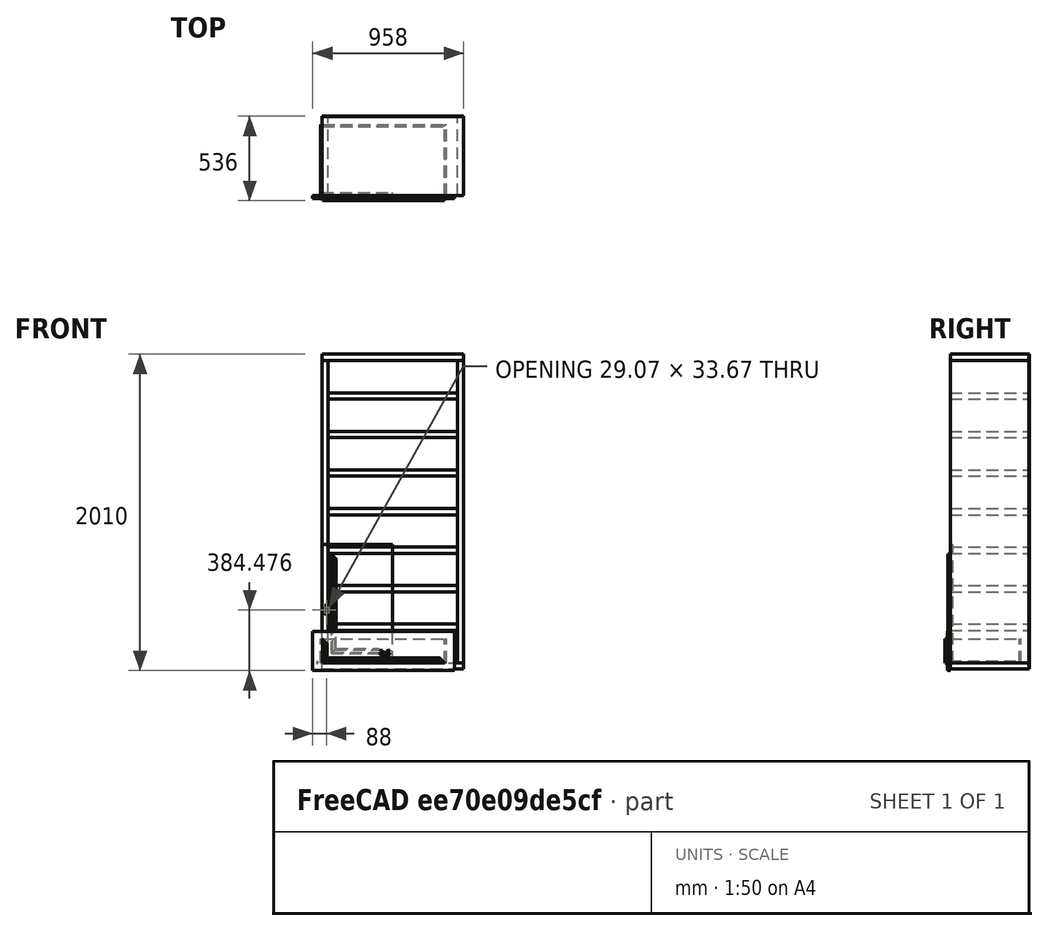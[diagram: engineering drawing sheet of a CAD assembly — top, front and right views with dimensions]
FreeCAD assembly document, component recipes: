
FREECAD ASSEMBLY — COMPONENT RECIPES ("Merged_002")

This assembly document has 18 components, labeled P0..P17 below (a component is one placed body or linked part). 9 of them carry a construction recipe — the FreeCAD feature program that regenerates the part from scratch, quoted from this document or its linked companion documents; the rest are supplied as boundary geometry only. No exploded tour is included for this assembly.
COMPONENT P0 — geometry summary ("Handle, Pin, Right"; no construction recipe available for this part):
  bounding box: 17.0 x 10.0 x 10.0 mm
  tessellated surface: 1,802 triangles
  volume: 817 mm^3 (48% of its bounding box)
  symmetry: revolution-symmetric about the y axis through its bounding-box center; mirror-symmetric across its x mid-plane, z mid-plane
COMPONENT P1 — geometry summary ("Link, Decoration, Top"; no construction recipe available for this part):
  bounding box: 776.0 x 30.0 x 15.0 mm
  tessellated surface: 126 triangles
  volume: 161274 mm^3 (46% of its bounding box)
  symmetry: mirror-symmetric across its x mid-plane
COMPONENT P2 — geometry summary ("Link, Decoration, Right"; no construction recipe available for this part):
  bounding box: 150.0 x 30.0 x 15.0 mm
  tessellated surface: 124 triangles
  volume: 27059 mm^3 (40% of its bounding box)
  symmetry: mirror-symmetric across its z mid-plane
COMPONENT P3 — geometry summary ("Link, Drawer"; no construction recipe available for this part):
  bounding box: 900.0 x 485.0 x 250.0 mm
  tessellated surface: 4,788 triangles
  volume: 8497740 mm^3 (8% of its bounding box)
  symmetry: mirror-symmetric across its x mid-plane
COMPONENT P4 — geometry summary ("Link, Segment 2"; no construction recipe available for this part):
  bounding box: 2000.0 x 901.0 x 538.0 mm
  tessellated surface: 15,092 triangles
  volume: 262938344 mm^3 (27% of its bounding box)
  symmetry: mirror-symmetric across its x mid-plane
COMPONENT P5 — geometry summary ("Link, Decoration, Top001"; no construction recipe available for this part):
  bounding box: 330.0 x 30.0 x 15.0 mm
  tessellated surface: 126 triangles
  volume: 65652 mm^3 (44% of its bounding box)
  symmetry: mirror-symmetric across its x mid-plane
COMPONENT P6 — geometry summary ("Link, Decoration, Right001"; no construction recipe available for this part):
  bounding box: 630.0 x 30.0 x 15.0 mm
  tessellated surface: 124 triangles
  volume: 129972 mm^3 (46% of its bounding box)
  symmetry: mirror-symmetric across its z mid-plane
COMPONENT P7 — geometry summary ("Link, Decoration, Top002"; no construction recipe available for this part):
  bounding box: 330.0 x 30.0 x 15.0 mm
  tessellated surface: 126 triangles
  volume: 65652 mm^3 (44% of its bounding box)
  symmetry: mirror-symmetric across its x mid-plane
COMPONENT P8 — geometry summary ("Link, Decoration, Right002"; no construction recipe available for this part):
  bounding box: 630.0 x 30.0 x 15.0 mm
  tessellated surface: 124 triangles
  volume: 129972 mm^3 (46% of its bounding box)
  symmetry: mirror-symmetric across its z mid-plane
COMPONENT P9 — recipe-attached ("Part, Handle", modeled in this document).
Construction recipe (the document's own serialized feature program — sketch geometry with constraints, then the solid features built on it; lengths are millimeters unless a unit is written):

FEATURE [Sketcher::SketchObject] Sketch006  label="Pattern, Handle"
  ArcFitTolerance = 0
  AttachmentOffset = pos=(400,75,28) rot=(0,0,1;0rad)
  AttachmentSupport = -> [XZ_Plane006]
  ExternalTypes = [0]
  FullyConstrained = true
  MakeInternals = false
  MapMode = 5
  Placement = pos=(400,-28,75) rot=(1,0,0;1.5708rad)
  _ExternalGeoVersion = 0
  expr: .AttachmentOffset.Base.x = <<settings>>.dwidth / 2
  expr: .AttachmentOffset.Base.y = <<settings>>.dheight / 2
  expr: .AttachmentOffset.Base.z = <<settings>>.fthick + 10 mm
  sketch-geometry (20):
    g0: LineSegment StartX=-31.5 StartY=2.62 StartZ=0 EndX=-17.57 EndY=2.62 EndZ=0
    g1: LineSegment StartX=-31.5 StartY=0 StartZ=0 EndX=-17.3512 EndY=0 EndZ=0
    g2: LineSegment StartX=-16.85 StartY=-2.15 StartZ=0 EndX=-28.7075 EndY=-12.82 EndZ=0
    g3: LineSegment StartX=-15.2654 StartY=-4.11 StartZ=0 EndX=-25.6265 EndY=-16.59 EndZ=0
    g4: LineSegment StartX=15.2654 StartY=-4.11 StartZ=0 EndX=25.6265 EndY=-16.59 EndZ=0
    g5: LineSegment StartX=16.85 StartY=-2.15 StartZ=0 EndX=28.7075 EndY=-12.82 EndZ=0
    g6: LineSegment StartX=17.57 StartY=2.62 StartZ=0 EndX=31.5 EndY=2.62 EndZ=0
    g7: LineSegment StartX=17.3512 StartY=0 StartZ=0 EndX=31.5 EndY=0 EndZ=0
    g8: LineSegment StartX=-10.78 StartY=-22.72 StartZ=0 EndX=10.78 EndY=-22.72 EndZ=0
    g9: LineSegment StartX=-31.5 StartY=2.62 StartZ=0 EndX=-31.5 EndY=0 EndZ=0
    g10: LineSegment StartX=31.5 StartY=2.62 StartZ=0 EndX=31.5 EndY=0 EndZ=0
    g11: ArcOfCircle CenterX=-17.98 CenterY=-1.28 CenterZ=0 NormalX=0 NormalY=0 NormalZ=1 AngleXU=0 Radius=3.92149 StartAngle=5.47698 EndAngle=7.74924
    g12: ArcOfCircle CenterX=-17.98 CenterY=-1.28 CenterZ=0 NormalX=0 NormalY=0 NormalZ=1 AngleXU=0 Radius=1.42611 StartAngle=5.62706 EndAngle=7.39735
    g13: ArcOfCircle CenterX=-19.81 CenterY=-17.89 CenterZ=0 NormalX=0 NormalY=0 NormalZ=1 AngleXU=0 Radius=10.2406 StartAngle=2.62366 EndAngle=5.79202
    g14: ArcOfCircle CenterX=19.81 CenterY=-17.89 CenterZ=0 NormalX=0 NormalY=0 NormalZ=1 AngleXU=0 Radius=10.2406 StartAngle=3.63276 EndAngle=6.80112
    g15: ArcOfCircle CenterX=17.98 CenterY=-1.28 CenterZ=0 NormalX=0 NormalY=0 NormalZ=1 AngleXU=0 Radius=3.92149 StartAngle=1.67554 EndAngle=3.9478
    g16: ArcOfCircle CenterX=17.98 CenterY=-1.28 CenterZ=0 NormalX=0 NormalY=0 NormalZ=1 AngleXU=0 Radius=1.42611 StartAngle=2.02742 EndAngle=3.79772
    g17: ArcOfCircle CenterX=0 CenterY=-24.02 CenterZ=0 NormalX=0 NormalY=0 NormalZ=1 AngleXU=0 Radius=14.7824 StartAngle=0.285269 EndAngle=2.85632
    g18: ArcOfCircle CenterX=-19.81 CenterY=-17.89 CenterZ=0 NormalX=0 NormalY=0 NormalZ=1 AngleXU=0 Radius=5.95999 StartAngle=2.9217 EndAngle=5.94631
    g19: ArcOfCircle CenterX=19.81 CenterY=-17.89 CenterZ=0 NormalX=0 NormalY=0 NormalZ=1 AngleXU=0 Radius=5.95999 StartAngle=3.47847 EndAngle=6.50307
  constraints (66):
    c: Horizontal(g0)
    c: Horizontal(g1)
    c: Horizontal(g6)
    c: Horizontal(g7)
    c: Horizontal(g8)
    c: Coincident(g9,g0)
    c: Coincident(g9,g1)
    c: Vertical(g9)
    c: Coincident(g10,g6)
    c: Vertical(g10)
    c: Coincident(g10,g7)
    c: Coincident(g11,g0)
    c: Coincident(g11,g3)
    c: Coincident(g12,g1)
    c: Coincident(g12,g2)
    c: Coincident(g13,g2)
    c: Coincident(g13,g8)
    c: Coincident(g14,g5)
    c: Coincident(g14,g8)
    c: Coincident(g15,g4)
    c: Coincident(g15,g6)
    c: Coincident(g16,g7)
    c: Coincident(g16,g5)
    c: Coincident(g18,g3)
    c: Coincident(g18,g17)
    c: Coincident(g19,g17)
    c: Coincident(g19,g4)
    c: Coincident(g15,g16)
    c: Coincident(g11,g12)
    c: Horizontal(g2,g5)
    c: Horizontal(g3,g4)
    c: Horizontal(g0,g6)
    c: Horizontal(g1,g7)
    c: Horizontal(g5,g2)
    c: Horizontal(g13,g14)
    c: Horizontal(g18,g19)
    c: Horizontal(g17,g17)
    c: Horizontal(g3,g4)
    c: PointOnObject(g17,g-2)
    c: Equal(g11,g15)
    c: Equal(g0,g6)
    c: Equal(g1,g7)
    c: Equal(g3,g4)
    c: Equal(g18,g19)
    c: Equal(g2,g5)
    c: Equal(g13,g14)
    c: Horizontal(g11,g15)
    c: Coincident(g13,g18)
    c: PointOnObject(g7,g-1)
    c: DistanceY(g17,g-1) = 24.02
    c: DistanceY(g14,g-1) = 17.89
    c: DistanceY(g2,g-1) = 12.82
    c: DistanceY(g3,g-1) = 16.59
    c: DistanceY(g8,g-1) = 22.72
    c: DistanceX(g8,g-1) = 10.78
    c: DistanceY(g3,g-1) = 4.11
    c: DistanceY(g2,g-1) = 2.15
    c: DistanceY(g-1,g0) = 2.62
    c: DistanceX(g0,g6) = 63
    c: DistanceX(g13,g14) = 39.62
    c: DistanceX(g17,g17) = 28.37
    c: DistanceY(g17,g-1) = 19.86
    c: DistanceX(g11,g-1) = 17.98
    c: DistanceX(g0,g-1) = 17.57
    c: DistanceX(g2,g-1) = 16.85
    c: DistanceY(g11,g-1) = 1.28
FEATURE [PartDesign::Pad] Pad006  label="Handle"
  Direction = (0,-1,2e-16)
  Length = 5
  Length2 = 10
  Placement = pos=(0,0,0) rot=(1,0,0;1.5708rad)
  Profile = -> Sketch006
  ReferenceAxis = -> Sketch006 [N_Axis]
  SideType = 0
  Suppressed = false
  Type = 0
  Type2 = 0
FEATURE [PartDesign::Body] Body006  label="Body, Handle"
  AllowCompound = true
  Group = -> [Sketch006,Pad006]
  Origin = -> Origin007
  Tip = -> Pad006
COMPONENT P10 — recipe-attached ("Part, Decoration, Bottom", modeled in this document).
Construction recipe (the document's own serialized feature program — sketch geometry with constraints, then the solid features built on it; lengths are millimeters unless a unit is written):

FEATURE [Sketcher::SketchObject] Sketch  label="Pattern, Decoration, Bottom"
  ArcFitTolerance = 0
  AttachmentOffset = pos=(-18,0,4) rot=(0,0,1;0rad)
  AttachmentSupport = -> [YZ_Plane008]
  ExternalTypes = [0]
  FullyConstrained = true
  MakeInternals = false
  MapMode = 5
  Placement = pos=(4,-18,0) rot=(0.57735,0.57735,0.57735;2.0944rad)
  _ExternalGeoVersion = 0
  expr: .AttachmentOffset.Base.x = -<<settings>>.fthick
  expr: .AttachmentOffset.Base.z = <<settings>>.bsink
  sketch-geometry (5):
    g0: LineSegment StartX=4e-16 StartY=30 StartZ=0 EndX=4e-16 EndY=0 EndZ=0
    g1: LineSegment StartX=4e-16 StartY=0 StartZ=0 EndX=-15 EndY=0 EndZ=0
    g2: ArcOfCircle CenterX=0 CenterY=23 CenterZ=0 NormalX=0 NormalY=0 NormalZ=1 AngleXU=0 Radius=7 StartAngle=1.5708 EndAngle=3.14159
    g3: ArcOfCircle CenterX=-16.3537 CenterY=15.4828 CenterZ=0 NormalX=0 NormalY=0 NormalZ=1 AngleXU=0 Radius=12 StartAngle=5.372 EndAngle=6.96016
    g4: ArcOfCircle CenterX=-9 CenterY=0 CenterZ=0 NormalX=0 NormalY=0 NormalZ=1 AngleXU=0 Radius=6 StartAngle=1.5708 EndAngle=3.14159
  constraints (17):
    c: Vertical(g0)
    c: Coincident(g1,g0)
    c: Horizontal(g1)
    c: Coincident(g2,g0)
    c: Coincident(g3,g2)
    c: Coincident(g4,g3)
    c: Coincident(g4,g1)
    c: DistanceY(g0,g0) = 30
    c: DistanceX(g1,g1) = 15
    c: Coincident(g0,g-1)
    c: PointOnObject(g2,g0)
    c: PointOnObject(g4,g1)
    c: Radius(g2) = 7
    c: Radius(g3) = 12
    c: Radius(g4) = 6
    c: Vertical(g3,g4)
    c: Horizontal(g2,g2)
FEATURE [PartDesign::Pad] Pad  label="Decoration, Bottom"
  Direction = (1,0,0)
  Length = 776
  Length2 = 10
  Placement = pos=(0,0,0) rot=(0.57735,0.57735,0.57735;2.0944rad)
  Profile = -> Sketch
  ReferenceAxis = -> Sketch [N_Axis]
  SideType = 0
  Suppressed = false
  Type = 0
  Type2 = 0
  expr: Length = <<settings>>.dwidth - 2 * <<settings>>.dthick
FEATURE [PartDesign::Body] Body  label="Body, Decoration, Bottom"
  AllowCompound = true
  Group = -> [Sketch,Pad]
  Origin = -> Origin009
  Tip = -> Pad
FEATURE [Sketcher::SketchObject] Sketch007  label="Pattern, Decoration, Bottom, Cut, Left"
  ArcFitTolerance = 0
  AttachmentOffset = pos=(4,0,18) rot=(0,0,1;0rad)
  AttachmentSupport = -> [XZ_Plane009]
  ExternalTypes = [0]
  FullyConstrained = true
  MakeInternals = false
  MapMode = 5
  Placement = pos=(4,-18,4e-15) rot=(1,0,0;1.5708rad)
  _ExternalGeoVersion = 0
  expr: .AttachmentOffset.Base.x = <<settings>>.bsink
  expr: .AttachmentOffset.Base.z = <<settings>>.fthick
  sketch-geometry (3):
    g0: LineSegment StartX=0 StartY=0 StartZ=0 EndX=40 EndY=40 EndZ=0
    g1: LineSegment StartX=40 StartY=40 StartZ=0 EndX=0 EndY=40 EndZ=0
    g2: LineSegment StartX=0 StartY=40 StartZ=0 EndX=0 EndY=0 EndZ=0
  constraints (8):
    c: Coincident(g0,g1)
    c: Horizontal(g1)
    c: Coincident(g1,g2)
    c: Coincident(g2,g0)
    c: Coincident(g0,g-1)
    c: Vertical(g2)
    c: Equal(g2,g1)
    c: DistanceY(g2,g2) = 40
FEATURE [PartDesign::Pad] Pad007  label="Decoration, Bottom, Cut, Left"
  Direction = (0,-1,2e-16)
  Length = 40
  Length2 = 10
  Placement = pos=(0,0,0) rot=(1,0,0;1.5708rad)
  Profile = -> Sketch007
  ReferenceAxis = -> Sketch007 [N_Axis]
  SideType = 0
  Suppressed = false
  Type = 0
  Type2 = 0
FEATURE [PartDesign::Body] Body007  label="Body, Decoration, Bottom, Cut, Left"
  AllowCompound = true
  Group = -> [Sketch007,Pad007]
  Origin = -> Origin010
  Tip = -> Pad007
FEATURE [Sketcher::SketchObject] Sketch008  label="Pattern, Decoration, Bottom, Cut, Right"
  ArcFitTolerance = 0
  AttachmentOffset = pos=(780,0,18) rot=(0,0,1;0rad)
  AttachmentSupport = -> [XZ_Plane010]
  ExternalTypes = [0]
  FullyConstrained = true
  MakeInternals = false
  MapMode = 5
  Placement = pos=(780,-18,4e-15) rot=(1,0,0;1.5708rad)
  _ExternalGeoVersion = 0
  expr: .AttachmentOffset.Base.x = <<settings>>.bsink + <<settings>>.dwidth - 2 * <<settings>>.dthick
  expr: .AttachmentOffset.Base.z = <<settings>>.fthick
  sketch-geometry (3):
    g0: LineSegment StartX=-40 StartY=40 StartZ=0 EndX=0 EndY=0 EndZ=0
    g1: LineSegment StartX=0 StartY=0 StartZ=0 EndX=0 EndY=40 EndZ=0
    g2: LineSegment StartX=0 StartY=40 StartZ=0 EndX=-40 EndY=40 EndZ=0
  constraints (8):
    c: Coincident(g0,g-1)
    c: Coincident(g0,g1)
    c: PointOnObject(g1,g-2)
    c: Coincident(g1,g2)
    c: Coincident(g2,g0)
    c: Horizontal(g2)
    c: Equal(g2,g1)
    c: DistanceY(g1,g1) = 40
FEATURE [PartDesign::Pad] Pad008  label="Decoration, Bottom, Cut, Right"
  Direction = (0,-1,2e-16)
  Length = 40
  Length2 = 10
  Placement = pos=(0,0,0) rot=(1,0,0;1.5708rad)
  Profile = -> Sketch008
  ReferenceAxis = -> Sketch008 [N_Axis]
  SideType = 0
  Suppressed = false
  Type = 0
  Type2 = 0
FEATURE [PartDesign::Body] Body008  label="Body, Decoration, Bottom, Cut, Right"
  AllowCompound = true
  Group = -> [Sketch008,Pad008]
  Origin = -> Origin011
  Tip = -> Pad008
COMPONENT P11 — recipe-attached ("Part, Decoration, Left", modeled in this document).
Construction recipe (the document's own serialized feature program — sketch geometry with constraints, then the solid features built on it; lengths are millimeters unless a unit is written):

FEATURE [Sketcher::SketchObject] Sketch009  label="Pattern, Decoration, Left"
  ArcFitTolerance = 0
  AttachmentOffset = pos=(4,-18,0) rot=(0,0,1;0rad)
  AttachmentSupport = -> [XY_Plane012]
  ExternalTypes = [0]
  FullyConstrained = true
  MakeInternals = false
  MapMode = 5
  Placement = pos=(4,-18,0) rot=(0,0,1;0rad)
  _ExternalGeoVersion = 0
  expr: .AttachmentOffset.Base.x = <<settings>>.bsink
  expr: .AttachmentOffset.Base.y = -<<settings>>.fthick
  sketch-geometry (5):
    g0: LineSegment StartX=30 StartY=-1.7e-15 StartZ=0 EndX=0 EndY=-1.7e-15 EndZ=0
    g1: LineSegment StartX=-1.1e-15 StartY=-15 StartZ=0 EndX=-1.1e-15 EndY=-1.8e-15 EndZ=0
    g2: ArcOfCircle CenterX=0 CenterY=-9 CenterZ=0 NormalX=0 NormalY=0 NormalZ=1 AngleXU=0 Radius=6 StartAngle=4.71239 EndAngle=6.28319
    g3: ArcOfCircle CenterX=15.4828 CenterY=-16.3537 CenterZ=0 NormalX=0 NormalY=0 NormalZ=1 AngleXU=0 Radius=12 StartAngle=0.893826 EndAngle=2.48198
    g4: ArcOfCircle CenterX=23 CenterY=0 CenterZ=0 NormalX=0 NormalY=0 NormalZ=1 AngleXU=0 Radius=7 StartAngle=4.71239 EndAngle=6.28319
  constraints (17):
    c: Vertical(g1)
    c: Coincident(g0,g1)
    c: Horizontal(g0)
    c: Coincident(g0,g-1)
    c: DistanceY(g1,g1) = 15
    c: DistanceX(g0,g0) = 30
    c: Coincident(g2,g1)
    c: Coincident(g3,g2)
    c: Coincident(g4,g3)
    c: Coincident(g4,g0)
    c: PointOnObject(g4,g0)
    c: PointOnObject(g2,g1)
    c: Radius(g2) = 6
    c: Radius(g3) = 12
    c: Radius(g4) = 7
    c: Horizontal(g2,g2)
    c: Vertical(g3,g4)
FEATURE [PartDesign::Pad] Pad009  label="Decoration, Left"
  Direction = (0,0,1)
  Length = 150
  Length2 = 10
  Profile = -> Sketch009
  ReferenceAxis = -> Sketch009 [N_Axis]
  SideType = 0
  Suppressed = false
  Type = 0
  Type2 = 0
  expr: Length = <<settings>>.dheight
FEATURE [PartDesign::Body] Body009  label="Body, Decoration, Left"
  AllowCompound = true
  Group = -> [Sketch009,Pad009]
  Origin = -> Origin013
  Tip = -> Pad009
FEATURE [Sketcher::SketchObject] Sketch010  label="Pattern, Decoration, Left, Cut, Bottom"
  ArcFitTolerance = 0
  AttachmentOffset = pos=(4,0,18) rot=(0,0,1;0rad)
  AttachmentSupport = -> [XZ_Plane013]
  ExternalTypes = [0]
  FullyConstrained = true
  MakeInternals = false
  MapMode = 5
  Placement = pos=(4,-18,4e-15) rot=(1,0,0;1.5708rad)
  _ExternalGeoVersion = 0
  expr: .AttachmentOffset.Base.x = <<settings>>.bsink
  expr: .AttachmentOffset.Base.z = <<settings>>.fthick
  sketch-geometry (3):
    g0: LineSegment StartX=0 StartY=0 StartZ=0 EndX=40 EndY=40 EndZ=0
    g1: LineSegment StartX=40 StartY=40 StartZ=0 EndX=40 EndY=0 EndZ=0
    g2: LineSegment StartX=40 StartY=0 StartZ=0 EndX=0 EndY=0 EndZ=0
  constraints (8):
    c: Coincident(g-1,g0)
    c: Coincident(g0,g1)
    c: PointOnObject(g1,g-1)
    c: Vertical(g1)
    c: Coincident(g1,g2)
    c: Coincident(g2,g0)
    c: Equal(g1,g2)
    c: DistanceY(g1,g1) = 40
FEATURE [PartDesign::Pad] Pad010  label="Decoration, Left, Cut, Bottom"
  Direction = (0,-1,2e-16)
  Length = 40
  Length2 = 10
  Placement = pos=(0,0,0) rot=(1,0,0;1.5708rad)
  Profile = -> Sketch010
  ReferenceAxis = -> Sketch010 [N_Axis]
  SideType = 0
  Suppressed = false
  Type = 0
  Type2 = 0
FEATURE [PartDesign::Body] Body010  label="Body, Decoration, Left, Cut, Bottom"
  AllowCompound = true
  Group = -> [Sketch010,Pad010]
  Origin = -> Origin014
  Tip = -> Pad010
FEATURE [Sketcher::SketchObject] Sketch011  label="Pattern, Decoration, Left, Cut, Top"
  ArcFitTolerance = 0
  AttachmentOffset = pos=(4,150,18) rot=(0,0,1;0rad)
  AttachmentSupport = -> [XZ_Plane014]
  ExternalTypes = [0]
  FullyConstrained = true
  MakeInternals = false
  MapMode = 5
  Placement = pos=(4,-18,150) rot=(1,0,0;1.5708rad)
  _ExternalGeoVersion = 0
  expr: .AttachmentOffset.Base.x = <<settings>>.bsink
  expr: .AttachmentOffset.Base.y = <<settings>>.dheight
  expr: .AttachmentOffset.Base.z = <<settings>>.fthick
  sketch-geometry (3):
    g0: LineSegment StartX=0 StartY=0 StartZ=0 EndX=40 EndY=-40 EndZ=0
    g1: LineSegment StartX=40 StartY=-40 StartZ=0 EndX=40 EndY=0 EndZ=0
    g2: LineSegment StartX=40 StartY=0 StartZ=0 EndX=0 EndY=0 EndZ=0
  constraints (8):
    c: Coincident(g-1,g0)
    c: Coincident(g0,g1)
    c: PointOnObject(g1,g-1)
    c: Vertical(g1)
    c: Coincident(g1,g2)
    c: Coincident(g2,g0)
    c: Equal(g1,g2)
    c: DistanceY(g1,g1) = 40
FEATURE [PartDesign::Pad] Pad011  label="Decoration, Left, Cut, Top"
  Direction = (0,-1,2e-16)
  Length = 40
  Length2 = 10
  Placement = pos=(0,0,0) rot=(1,0,0;1.5708rad)
  Profile = -> Sketch011
  ReferenceAxis = -> Sketch011 [N_Axis]
  SideType = 0
  Suppressed = false
  Type = 0
  Type2 = 0
FEATURE [PartDesign::Body] Body011  label="Body, Decoration, Left, Cut, Top"
  AllowCompound = true
  Group = -> [Sketch011,Pad011]
  Origin = -> Origin015
  Tip = -> Pad011
COMPONENT P12 — recipe-attached ("Part, Decoration, Bottom001", modeled in this document).
Construction recipe (the document's own serialized feature program — sketch geometry with constraints, then the solid features built on it; lengths are millimeters unless a unit is written):

FEATURE [Sketcher::SketchObject] Sketch012  label="Pattern, Decoration, Bottom001"
  ArcFitTolerance = 0
  AttachmentOffset = pos=(0,60,60) rot=(0,0,1;0rad)
  AttachmentSupport = -> [YZ_Plane016]
  ExternalTypes = [0]
  FullyConstrained = true
  MakeInternals = false
  MapMode = 5
  Placement = pos=(60,0,60) rot=(0.57735,0.57735,0.57735;2.0944rad)
  _ExternalGeoVersion = 0
  expr: .AttachmentOffset.Base.y = Spreadsheet001.frdoffset
  expr: .AttachmentOffset.Base.z = Spreadsheet001.frdoffset
  sketch-geometry (5):
    g0: LineSegment StartX=4e-16 StartY=30 StartZ=0 EndX=4e-16 EndY=0 EndZ=0
    g1: LineSegment StartX=4e-16 StartY=0 StartZ=0 EndX=-15 EndY=0 EndZ=0
    g2: ArcOfCircle CenterX=0 CenterY=23 CenterZ=0 NormalX=0 NormalY=0 NormalZ=1 AngleXU=0 Radius=7 StartAngle=1.5708 EndAngle=3.14159
    g3: ArcOfCircle CenterX=-16.3537 CenterY=15.4828 CenterZ=0 NormalX=0 NormalY=0 NormalZ=1 AngleXU=0 Radius=12 StartAngle=5.372 EndAngle=6.96016
    g4: ArcOfCircle CenterX=-9 CenterY=0 CenterZ=0 NormalX=0 NormalY=0 NormalZ=1 AngleXU=0 Radius=6 StartAngle=1.5708 EndAngle=3.14159
  constraints (17):
    c: Vertical(g0)
    c: Coincident(g1,g0)
    c: Horizontal(g1)
    c: Coincident(g2,g0)
    c: Coincident(g3,g2)
    c: Coincident(g4,g3)
    c: Coincident(g4,g1)
    c: DistanceY(g0,g0) = 30
    c: DistanceX(g1,g1) = 15
    c: Coincident(g0,g-1)
    c: PointOnObject(g2,g0)
    c: PointOnObject(g4,g1)
    c: Radius(g2) = 7
    c: Radius(g3) = 12
    c: Radius(g4) = 6
    c: Vertical(g3,g4)
    c: Horizontal(g2,g2)
FEATURE [PartDesign::Pad] Pad012  label="Decoration, Bottom001"
  Direction = (1,0,0)
  Length = 330
  Length2 = 10
  Placement = pos=(0,0,0) rot=(0.57735,0.57735,0.57735;2.0944rad)
  Profile = -> Sketch012
  ReferenceAxis = -> Sketch012 [N_Axis]
  SideType = 0
  Suppressed = false
  Type = 0
  Type2 = 0
  expr: Length = Spreadsheet001.frfwidth - 2 * Spreadsheet001.frdoffset
FEATURE [PartDesign::Body] Body012  label="Body, Decoration, Bottom001"
  AllowCompound = true
  Group = -> [Sketch012,Pad012]
  Origin = -> Origin017
  Tip = -> Pad012
FEATURE [Sketcher::SketchObject] Sketch013  label="Pattern, Decoration, Bottom, Cut, Left001"
  ArcFitTolerance = 0
  AttachmentOffset = pos=(60,60,0) rot=(0,0,1;0rad)
  AttachmentSupport = -> [XZ_Plane017]
  ExternalTypes = [0]
  FullyConstrained = true
  MakeInternals = false
  MapMode = 5
  Placement = pos=(60,1.33e-14,60) rot=(1,0,0;1.5708rad)
  _ExternalGeoVersion = 0
  expr: .AttachmentOffset.Base.x = Spreadsheet001.frdoffset
  expr: .AttachmentOffset.Base.y = Spreadsheet001.frdoffset
  sketch-geometry (3):
    g0: LineSegment StartX=0 StartY=0 StartZ=0 EndX=40 EndY=40 EndZ=0
    g1: LineSegment StartX=40 StartY=40 StartZ=0 EndX=0 EndY=40 EndZ=0
    g2: LineSegment StartX=0 StartY=40 StartZ=0 EndX=0 EndY=0 EndZ=0
  constraints (8):
    c: Coincident(g0,g1)
    c: Horizontal(g1)
    c: Coincident(g1,g2)
    c: Coincident(g2,g0)
    c: Coincident(g0,g-1)
    c: Vertical(g2)
    c: Equal(g2,g1)
    c: DistanceY(g2,g2) = 40
FEATURE [PartDesign::Pad] Pad013  label="Decoration, Bottom, Cut, Left001"
  Direction = (0,-1,2e-16)
  Length = 40
  Length2 = 10
  Placement = pos=(0,0,0) rot=(1,0,0;1.5708rad)
  Profile = -> Sketch013
  ReferenceAxis = -> Sketch013 [N_Axis]
  SideType = 0
  Suppressed = false
  Type = 0
  Type2 = 0
FEATURE [PartDesign::Body] Body013  label="Body, Decoration, Bottom, Cut, Left001"
  AllowCompound = true
  Group = -> [Sketch013,Pad013]
  Origin = -> Origin018
  Tip = -> Pad013
FEATURE [Sketcher::SketchObject] Sketch014  label="Pattern, Decoration, Bottom, Cut, Right001"
  ArcFitTolerance = 0
  AttachmentOffset = pos=(390,60,0) rot=(0,0,1;0rad)
  AttachmentSupport = -> [XZ_Plane018]
  ExternalTypes = [0]
  FullyConstrained = true
  MakeInternals = false
  MapMode = 5
  Placement = pos=(390,1.33e-14,60) rot=(1,0,0;1.5708rad)
  _ExternalGeoVersion = 0
  expr: .AttachmentOffset.Base.x = Spreadsheet001.frfwidth - Spreadsheet001.frdoffset
  expr: .AttachmentOffset.Base.y = Spreadsheet001.frdoffset
  sketch-geometry (3):
    g0: LineSegment StartX=-40 StartY=40 StartZ=0 EndX=0 EndY=0 EndZ=0
    g1: LineSegment StartX=0 StartY=0 StartZ=0 EndX=0 EndY=40 EndZ=0
    g2: LineSegment StartX=0 StartY=40 StartZ=0 EndX=-40 EndY=40 EndZ=0
  constraints (8):
    c: Coincident(g0,g-1)
    c: Coincident(g0,g1)
    c: PointOnObject(g1,g-2)
    c: Coincident(g1,g2)
    c: Coincident(g2,g0)
    c: Horizontal(g2)
    c: Equal(g2,g1)
    c: DistanceY(g1,g1) = 40
FEATURE [PartDesign::Pad] Pad014  label="Decoration, Bottom, Cut, Right001"
  Direction = (0,-1,2e-16)
  Length = 40
  Length2 = 10
  Placement = pos=(0,0,0) rot=(1,0,0;1.5708rad)
  Profile = -> Sketch014
  ReferenceAxis = -> Sketch014 [N_Axis]
  SideType = 0
  Suppressed = false
  Type = 0
  Type2 = 0
FEATURE [PartDesign::Body] Body014  label="Body, Decoration, Bottom, Cut, Right001"
  AllowCompound = true
  Group = -> [Sketch014,Pad014]
  Origin = -> Origin019
  Tip = -> Pad014
COMPONENT P13 — recipe-attached ("Part, Decoration, Left001", modeled in this document).
Construction recipe (the document's own serialized feature program — sketch geometry with constraints, then the solid features built on it; lengths are millimeters unless a unit is written):

FEATURE [Sketcher::SketchObject] Sketch015  label="Pattern, Decoration, Left001"
  ArcFitTolerance = 0
  AttachmentOffset = pos=(60,0,60) rot=(0,0,1;0rad)
  AttachmentSupport = -> [XY_Plane020]
  ExternalTypes = [0]
  FullyConstrained = true
  MakeInternals = false
  MapMode = 5
  Placement = pos=(60,0,60) rot=(0,0,1;0rad)
  _ExternalGeoVersion = 0
  expr: .AttachmentOffset.Base.x = Spreadsheet001.frdoffset
  expr: .AttachmentOffset.Base.z = Spreadsheet001.frdoffset
  sketch-geometry (5):
    g0: LineSegment StartX=30 StartY=-1.8e-15 StartZ=0 EndX=0 EndY=-1.8e-15 EndZ=0
    g1: LineSegment StartX=0 StartY=-15 StartZ=0 EndX=0 EndY=-1.8e-15 EndZ=0
    g2: ArcOfCircle CenterX=0 CenterY=-9 CenterZ=0 NormalX=0 NormalY=0 NormalZ=1 AngleXU=0 Radius=6 StartAngle=4.71239 EndAngle=6.28319
    g3: ArcOfCircle CenterX=15.4828 CenterY=-16.3537 CenterZ=0 NormalX=0 NormalY=0 NormalZ=1 AngleXU=0 Radius=12 StartAngle=0.893826 EndAngle=2.48198
    g4: ArcOfCircle CenterX=23 CenterY=0 CenterZ=0 NormalX=0 NormalY=0 NormalZ=1 AngleXU=0 Radius=7 StartAngle=4.71239 EndAngle=6.28319
  constraints (17):
    c: Vertical(g1)
    c: Coincident(g0,g1)
    c: Horizontal(g0)
    c: Coincident(g0,g-1)
    c: DistanceY(g1,g1) = 15
    c: DistanceX(g0,g0) = 30
    c: Coincident(g2,g1)
    c: Coincident(g3,g2)
    c: Coincident(g4,g3)
    c: Coincident(g4,g0)
    c: PointOnObject(g4,g0)
    c: PointOnObject(g2,g1)
    c: Radius(g2) = 6
    c: Radius(g3) = 12
    c: Radius(g4) = 7
    c: Horizontal(g2,g2)
    c: Vertical(g3,g4)
FEATURE [PartDesign::Pad] Pad015  label="Decoration, Left001"
  Direction = (0,0,1)
  Length = 630
  Length2 = 10
  Profile = -> Sketch015
  ReferenceAxis = -> Sketch015 [N_Axis]
  SideType = 0
  Suppressed = false
  Type = 0
  Type2 = 0
  expr: Length = Spreadsheet001.frfheight - 2 * Spreadsheet001.frdoffset
FEATURE [PartDesign::Body] Body015  label="Body, Decoration, Left001"
  AllowCompound = true
  Group = -> [Sketch015,Pad015]
  Origin = -> Origin021
  Tip = -> Pad015
FEATURE [Sketcher::SketchObject] Sketch016  label="Pattern, Decoration, Left, Cut, Bottom001"
  ArcFitTolerance = 0
  AttachmentOffset = pos=(60,60,0) rot=(0,0,1;0rad)
  AttachmentSupport = -> [XZ_Plane021]
  ExternalTypes = [0]
  FullyConstrained = true
  MakeInternals = false
  MapMode = 5
  Placement = pos=(60,1.33e-14,60) rot=(1,0,0;1.5708rad)
  _ExternalGeoVersion = 0
  expr: .AttachmentOffset.Base.x = Spreadsheet001.frdoffset
  expr: .AttachmentOffset.Base.y = Spreadsheet001.frdoffset
  sketch-geometry (3):
    g0: LineSegment StartX=0 StartY=0 StartZ=0 EndX=40 EndY=40 EndZ=0
    g1: LineSegment StartX=40 StartY=40 StartZ=0 EndX=40 EndY=0 EndZ=0
    g2: LineSegment StartX=40 StartY=0 StartZ=0 EndX=0 EndY=0 EndZ=0
  constraints (8):
    c: Coincident(g-1,g0)
    c: Coincident(g0,g1)
    c: PointOnObject(g1,g-1)
    c: Vertical(g1)
    c: Coincident(g1,g2)
    c: Coincident(g2,g0)
    c: Equal(g1,g2)
    c: DistanceY(g1,g1) = 40
FEATURE [PartDesign::Pad] Pad016  label="Decoration, Left, Cut, Bottom001"
  Direction = (0,-1,2e-16)
  Length = 40
  Length2 = 10
  Placement = pos=(0,0,0) rot=(1,0,0;1.5708rad)
  Profile = -> Sketch016
  ReferenceAxis = -> Sketch016 [N_Axis]
  SideType = 0
  Suppressed = false
  Type = 0
  Type2 = 0
FEATURE [PartDesign::Body] Body016  label="Body, Decoration, Left, Cut, Bottom001"
  AllowCompound = true
  Group = -> [Sketch016,Pad016]
  Origin = -> Origin022
  Tip = -> Pad016
FEATURE [Sketcher::SketchObject] Sketch017  label="Pattern, Decoration, Left, Cut, Top001"
  ArcFitTolerance = 0
  AttachmentOffset = pos=(60,690,0) rot=(0,0,1;0rad)
  AttachmentSupport = -> [XZ_Plane022]
  ExternalTypes = [0]
  FullyConstrained = true
  MakeInternals = false
  MapMode = 5
  Placement = pos=(60,1.532e-13,690) rot=(1,0,0;1.5708rad)
  _ExternalGeoVersion = 0
  expr: .AttachmentOffset.Base.x = Spreadsheet001.frdoffset
  expr: .AttachmentOffset.Base.y = Spreadsheet001.frfheight - Spreadsheet001.frdoffset
  sketch-geometry (3):
    g0: LineSegment StartX=0 StartY=0 StartZ=0 EndX=40 EndY=-40 EndZ=0
    g1: LineSegment StartX=40 StartY=-40 StartZ=0 EndX=40 EndY=0 EndZ=0
    g2: LineSegment StartX=40 StartY=0 StartZ=0 EndX=0 EndY=0 EndZ=0
  constraints (8):
    c: Coincident(g-1,g0)
    c: Coincident(g0,g1)
    c: PointOnObject(g1,g-1)
    c: Vertical(g1)
    c: Coincident(g1,g2)
    c: Coincident(g2,g0)
    c: Equal(g1,g2)
    c: DistanceY(g1,g1) = 40
FEATURE [PartDesign::Pad] Pad017  label="Decoration, Left, Cut, Top001"
  Direction = (0,-1,2e-16)
  Length = 40
  Length2 = 10
  Placement = pos=(0,0,0) rot=(1,0,0;1.5708rad)
  Profile = -> Sketch017
  ReferenceAxis = -> Sketch017 [N_Axis]
  SideType = 0
  Suppressed = false
  Type = 0
  Type2 = 0
FEATURE [PartDesign::Body] Body017  label="Body, Decoration, Left, Cut, Top001"
  AllowCompound = true
  Group = -> [Sketch017,Pad017]
  Origin = -> Origin023
  Tip = -> Pad017
COMPONENT P14 — recipe-attached ("Part, Handle001", modeled in this document).
Construction recipe (the document's own serialized feature program — sketch geometry with constraints, then the solid features built on it; lengths are millimeters unless a unit is written):

FEATURE [Sketcher::SketchObject] Sketch018  label="Sketch012"
  ArcFitTolerance = 0
  AttachmentOffset = pos=(30,375,8) rot=(0,0,1;0rad)
  AttachmentSupport = -> [XZ_Plane024]
  ExternalTypes = [0]
  FullyConstrained = true
  MakeInternals = false
  MapMode = 5
  Placement = pos=(30,-8,375) rot=(1,0,0;1.5708rad)
  _ExternalGeoVersion = 0
  expr: .AttachmentOffset.Base.x = Spreadsheet001.frdoffset / 2
  expr: .AttachmentOffset.Base.y = Spreadsheet001.frfheight / 2
  sketch-geometry (13):
    g0: LineSegment StartX=-2.89 StartY=0 StartZ=0 EndX=-2.89 EndY=-20 EndZ=0
    g1: LineSegment StartX=2.89 StartY=0 StartZ=0 EndX=2.89 EndY=-20 EndZ=0
    g2: LineSegment StartX=-2.89 StartY=0 StartZ=0 EndX=2.89 EndY=0 EndZ=0
    g3: LineSegment StartX=-2.89 StartY=-20 StartZ=0 EndX=-20.5255 EndY=-49.48 EndZ=0
    g4: LineSegment StartX=2.89 StartY=-20 StartZ=0 EndX=20.5255 EndY=-49.48 EndZ=0
    g5: LineSegment StartX=-13.7655 StartY=-48.2802 StartZ=0 EndX=0 EndY=-23.6879 EndZ=0
    g6: LineSegment StartX=0 StartY=-23.6879 StartZ=0 EndX=13.7655 EndY=-48.2802 EndZ=0
    g7: ArcOfCircle CenterX=-7.79 CenterY=-51.47 CenterZ=0 NormalX=0 NormalY=0 NormalZ=1 AngleXU=0 Radius=12.89 StartAngle=2.98659 EndAngle=4.71316
    g8: ArcOfCircle CenterX=-7.79 CenterY=-51.47 CenterZ=0 NormalX=0 NormalY=0 NormalZ=1 AngleXU=0 Radius=6.77356 StartAngle=2.65126 EndAngle=4.1959
    g9: ArcOfCircle CenterX=0 CenterY=-62.5379 CenterZ=0 NormalX=0 NormalY=0 NormalZ=1 AngleXU=0 Radius=12.28 StartAngle=0.435264 EndAngle=2.70633
    g10: ArcOfCircle CenterX=7.79 CenterY=-51.47 CenterZ=0 NormalX=0 NormalY=0 NormalZ=1 AngleXU=0 Radius=6.77356 StartAngle=5.22888 EndAngle=6.77352
    g11: ArcOfCircle CenterX=7.79 CenterY=-51.47 CenterZ=0 NormalX=0 NormalY=0 NormalZ=1 AngleXU=0 Radius=12.89 StartAngle=4.71316 EndAngle=6.43819
    g12: LineSegment StartX=-7.78 StartY=-64.36 StartZ=0 EndX=7.8 EndY=-64.36 EndZ=0
  constraints (42):
    c: PointOnObject(g0,g-1)
    c: Vertical(g0)
    c: PointOnObject(g1,g-1)
    c: Vertical(g1)
    c: Coincident(g2,g0)
    c: Coincident(g2,g1)
    c: Coincident(g3,g0)
    c: Coincident(g4,g1)
    c: PointOnObject(g5,g-2)
    c: Coincident(g6,g5)
    c: Coincident(g7,g3)
    c: Coincident(g8,g5)
    c: Coincident(g9,g8)
    c: Coincident(g10,g9)
    c: Coincident(g10,g6)
    c: Coincident(g11,g4)
    c: Coincident(g12,g7)
    c: Coincident(g12,g11)
    c: Horizontal(g12)
    c: DistanceY(g1,g1) = 20
    c: Equal(g0,g1)
    c: Equal(g3,g4)
    c: Equal(g5,g6)
    c: Equal(g8,g10)
    c: Equal(g7,g11)
    c: PointOnObject(g9,g-2)
    c: Horizontal(g9,g8)
    c: Horizontal(g3,g4)
    c: Horizontal(g5,g6)
    c: Coincident(g7,g8)
    c: Coincident(g10,g11)
    c: DistanceX(g0,g-1) = 2.89
    c: DistanceX(g3,g5) = 6.76
    c: DistanceY(g9,g5) = 38.85
    c: DistanceY(g7,g-1) = 64.36
    c: DistanceY(g7,g-1) = 51.47
    c: DistanceX(g8,g9) = 22.27
    c: DistanceX(g9,g10) = 7.79
    c: DistanceY(g9,g-1) = 57.36
    c: DistanceY(g4,g-1) = 49.48
    c: DistanceX(g9,g11) = 7.8
    c: Radius(g9) = 12.28
FEATURE [PartDesign::Pad] Pad018  label="Handle001"
  Direction = (0,-1,2e-16)
  Length = 5
  Length2 = 10
  Placement = pos=(0,0,0) rot=(1,0,0;1.5708rad)
  Profile = -> Sketch018
  ReferenceAxis = -> Sketch018 [N_Axis]
  SideType = 0
  Suppressed = false
  Type = 0
  Type2 = 0
FEATURE [PartDesign::Body] Body018  label="Body, Handle001"
  AllowCompound = true
  Group = -> [Sketch018,Pad018]
  Origin = -> Origin025
  Tip = -> Pad018
COMPONENT P15 — recipe-attached ("Part, Decoration, Bottom002", modeled in this document).
Construction recipe (the document's own serialized feature program — sketch geometry with constraints, then the solid features built on it; lengths are millimeters unless a unit is written):

FEATURE [Sketcher::SketchObject] Sketch019  label="Pattern, Decoration, Bottom002"
  ArcFitTolerance = 0
  AttachmentOffset = pos=(0,60,60) rot=(0,0,1;0rad)
  AttachmentSupport = -> [YZ_Plane026]
  ExternalTypes = [0]
  FullyConstrained = true
  MakeInternals = false
  MapMode = 5
  Placement = pos=(60,0,60) rot=(0.57735,0.57735,0.57735;2.0944rad)
  _ExternalGeoVersion = 0
  expr: .AttachmentOffset.Base.y = Spreadsheet002.fldoffset
  expr: .AttachmentOffset.Base.z = Spreadsheet002.fldoffset
  sketch-geometry (5):
    g0: LineSegment StartX=4e-16 StartY=30 StartZ=0 EndX=4e-16 EndY=0 EndZ=0
    g1: LineSegment StartX=4e-16 StartY=7e-16 StartZ=0 EndX=-15 EndY=7e-16 EndZ=0
    g2: ArcOfCircle CenterX=0 CenterY=23 CenterZ=0 NormalX=0 NormalY=0 NormalZ=1 AngleXU=0 Radius=7 StartAngle=1.5708 EndAngle=3.14159
    g3: ArcOfCircle CenterX=-16.3537 CenterY=15.4828 CenterZ=0 NormalX=0 NormalY=0 NormalZ=1 AngleXU=0 Radius=12 StartAngle=5.372 EndAngle=6.96016
    g4: ArcOfCircle CenterX=-9 CenterY=0 CenterZ=0 NormalX=0 NormalY=0 NormalZ=1 AngleXU=0 Radius=6 StartAngle=1.5708 EndAngle=3.14159
  constraints (17):
    c: Vertical(g0)
    c: Coincident(g1,g0)
    c: Horizontal(g1)
    c: Coincident(g2,g0)
    c: Coincident(g3,g2)
    c: Coincident(g4,g3)
    c: Coincident(g4,g1)
    c: DistanceY(g0,g0) = 30
    c: DistanceX(g1,g1) = 15
    c: Coincident(g0,g-1)
    c: PointOnObject(g2,g0)
    c: PointOnObject(g4,g1)
    c: Radius(g2) = 7
    c: Radius(g3) = 12
    c: Radius(g4) = 6
    c: Vertical(g3,g4)
    c: Horizontal(g2,g2)
FEATURE [PartDesign::Pad] Pad019  label="Decoration, Bottom002"
  Direction = (1,0,0)
  Length = 330
  Length2 = 10
  Placement = pos=(0,0,0) rot=(0.57735,0.57735,0.57735;2.0944rad)
  Profile = -> Sketch019
  ReferenceAxis = -> Sketch019 [N_Axis]
  SideType = 0
  Suppressed = false
  Type = 0
  Type2 = 0
  expr: Length = Spreadsheet002.flfwidth - 2 * Spreadsheet002.fldoffset
FEATURE [PartDesign::Body] Body019  label="Body, Decoration, Bottom002"
  AllowCompound = true
  Group = -> [Sketch019,Pad019]
  Origin = -> Origin027
  Tip = -> Pad019
FEATURE [Sketcher::SketchObject] Sketch020  label="Pattern, Decoration, Bottom, Cut, Left002"
  ArcFitTolerance = 0
  AttachmentOffset = pos=(60,60,0) rot=(0,0,1;0rad)
  AttachmentSupport = -> [XZ_Plane027]
  ExternalTypes = [0]
  FullyConstrained = true
  MakeInternals = false
  MapMode = 5
  Placement = pos=(60,1.33e-14,60) rot=(1,0,0;1.5708rad)
  _ExternalGeoVersion = 0
  expr: .AttachmentOffset.Base.x = Spreadsheet002.fldoffset
  expr: .AttachmentOffset.Base.y = Spreadsheet002.fldoffset
  sketch-geometry (3):
    g0: LineSegment StartX=0 StartY=0 StartZ=0 EndX=40 EndY=40 EndZ=0
    g1: LineSegment StartX=40 StartY=40 StartZ=0 EndX=0 EndY=40 EndZ=0
    g2: LineSegment StartX=0 StartY=40 StartZ=0 EndX=0 EndY=0 EndZ=0
  constraints (8):
    c: Coincident(g0,g1)
    c: Horizontal(g1)
    c: Coincident(g1,g2)
    c: Coincident(g2,g0)
    c: Coincident(g0,g-1)
    c: Vertical(g2)
    c: Equal(g2,g1)
    c: DistanceY(g2,g2) = 40
FEATURE [PartDesign::Pad] Pad020  label="Decoration, Bottom, Cut, Left002"
  Direction = (0,-1,2e-16)
  Length = 40
  Length2 = 10
  Placement = pos=(0,0,0) rot=(1,0,0;1.5708rad)
  Profile = -> Sketch020
  ReferenceAxis = -> Sketch020 [N_Axis]
  SideType = 0
  Suppressed = false
  Type = 0
  Type2 = 0
FEATURE [PartDesign::Body] Body020  label="Body, Decoration, Bottom, Cut, Left002"
  AllowCompound = true
  Group = -> [Sketch020,Pad020]
  Origin = -> Origin028
  Tip = -> Pad020
FEATURE [Sketcher::SketchObject] Sketch021  label="Pattern, Decoration, Bottom, Cut, Right002"
  ArcFitTolerance = 0
  AttachmentOffset = pos=(390,60,0) rot=(0,0,1;0rad)
  AttachmentSupport = -> [XZ_Plane028]
  ExternalTypes = [0]
  FullyConstrained = true
  MakeInternals = false
  MapMode = 5
  Placement = pos=(390,1.33e-14,60) rot=(1,0,0;1.5708rad)
  _ExternalGeoVersion = 0
  expr: .AttachmentOffset.Base.x = Spreadsheet002.flfwidth - Spreadsheet002.fldoffset
  expr: .AttachmentOffset.Base.y = Spreadsheet002.fldoffset
  sketch-geometry (3):
    g0: LineSegment StartX=-40 StartY=40 StartZ=0 EndX=0 EndY=0 EndZ=0
    g1: LineSegment StartX=0 StartY=0 StartZ=0 EndX=0 EndY=40 EndZ=0
    g2: LineSegment StartX=0 StartY=40 StartZ=0 EndX=-40 EndY=40 EndZ=0
  constraints (8):
    c: Coincident(g0,g-1)
    c: Coincident(g0,g1)
    c: PointOnObject(g1,g-2)
    c: Coincident(g1,g2)
    c: Coincident(g2,g0)
    c: Horizontal(g2)
    c: Equal(g2,g1)
    c: DistanceY(g1,g1) = 40
FEATURE [PartDesign::Pad] Pad021  label="Decoration, Bottom, Cut, Right002"
  Direction = (0,-1,2e-16)
  Length = 40
  Length2 = 10
  Placement = pos=(0,0,0) rot=(1,0,0;1.5708rad)
  Profile = -> Sketch021
  ReferenceAxis = -> Sketch021 [N_Axis]
  SideType = 0
  Suppressed = false
  Type = 0
  Type2 = 0
FEATURE [PartDesign::Body] Body021  label="Body, Decoration, Bottom, Cut, Right002"
  AllowCompound = true
  Group = -> [Sketch021,Pad021]
  Origin = -> Origin029
  Tip = -> Pad021
COMPONENT P16 — recipe-attached ("Part, Decoration, Left002", modeled in this document).
Construction recipe (the document's own serialized feature program — sketch geometry with constraints, then the solid features built on it; lengths are millimeters unless a unit is written):

FEATURE [Sketcher::SketchObject] Sketch022  label="Pattern, Decoration, Left002"
  ArcFitTolerance = 0
  AttachmentOffset = pos=(60,0,60) rot=(0,0,1;0rad)
  AttachmentSupport = -> [XY_Plane030]
  ExternalTypes = [0]
  FullyConstrained = true
  MakeInternals = false
  MapMode = 5
  Placement = pos=(60,0,60) rot=(0,0,1;0rad)
  _ExternalGeoVersion = 0
  expr: .AttachmentOffset.Base.x = Spreadsheet002.fldoffset
  expr: .AttachmentOffset.Base.z = Spreadsheet002.fldoffset
  sketch-geometry (5):
    g0: LineSegment StartX=30 StartY=-1.7e-15 StartZ=0 EndX=0 EndY=-1.7e-15 EndZ=0
    g1: LineSegment StartX=0 StartY=-15 StartZ=0 EndX=0 EndY=-1.8e-15 EndZ=0
    g2: ArcOfCircle CenterX=0 CenterY=-9 CenterZ=0 NormalX=0 NormalY=0 NormalZ=1 AngleXU=0 Radius=6 StartAngle=4.71239 EndAngle=6.28319
    g3: ArcOfCircle CenterX=15.4828 CenterY=-16.3537 CenterZ=0 NormalX=0 NormalY=0 NormalZ=1 AngleXU=0 Radius=12 StartAngle=0.893826 EndAngle=2.48198
    g4: ArcOfCircle CenterX=23 CenterY=0 CenterZ=0 NormalX=0 NormalY=0 NormalZ=1 AngleXU=0 Radius=7 StartAngle=4.71239 EndAngle=6.28319
  constraints (17):
    c: Vertical(g1)
    c: Coincident(g0,g1)
    c: Horizontal(g0)
    c: Coincident(g0,g-1)
    c: DistanceY(g1,g1) = 15
    c: DistanceX(g0,g0) = 30
    c: Coincident(g2,g1)
    c: Coincident(g3,g2)
    c: Coincident(g4,g3)
    c: Coincident(g4,g0)
    c: PointOnObject(g4,g0)
    c: PointOnObject(g2,g1)
    c: Radius(g2) = 6
    c: Radius(g3) = 12
    c: Radius(g4) = 7
    c: Horizontal(g2,g2)
    c: Vertical(g3,g4)
FEATURE [PartDesign::Pad] Pad022  label="Decoration, Left002"
  Direction = (0,0,1)
  Length = 630
  Length2 = 10
  Profile = -> Sketch022
  ReferenceAxis = -> Sketch022 [N_Axis]
  SideType = 0
  Suppressed = false
  Type = 0
  Type2 = 0
  expr: Length = Spreadsheet002.flfheight - 2 * Spreadsheet002.fldoffset
FEATURE [PartDesign::Body] Body022  label="Body, Decoration, Left002"
  AllowCompound = true
  Group = -> [Sketch022,Pad022]
  Origin = -> Origin031
  Tip = -> Pad022
FEATURE [Sketcher::SketchObject] Sketch023  label="Pattern, Decoration, Left, Cut, Bottom002"
  ArcFitTolerance = 0
  AttachmentOffset = pos=(60,60,0) rot=(0,0,1;0rad)
  AttachmentSupport = -> [XZ_Plane031]
  ExternalTypes = [0]
  FullyConstrained = true
  MakeInternals = false
  MapMode = 5
  Placement = pos=(60,1.33e-14,60) rot=(1,0,0;1.5708rad)
  _ExternalGeoVersion = 0
  expr: .AttachmentOffset.Base.x = Spreadsheet002.fldoffset
  expr: .AttachmentOffset.Base.y = Spreadsheet002.fldoffset
  sketch-geometry (3):
    g0: LineSegment StartX=0 StartY=0 StartZ=0 EndX=40 EndY=40 EndZ=0
    g1: LineSegment StartX=40 StartY=40 StartZ=0 EndX=40 EndY=0 EndZ=0
    g2: LineSegment StartX=40 StartY=0 StartZ=0 EndX=0 EndY=0 EndZ=0
  constraints (8):
    c: Coincident(g-1,g0)
    c: Coincident(g0,g1)
    c: PointOnObject(g1,g-1)
    c: Vertical(g1)
    c: Coincident(g1,g2)
    c: Coincident(g2,g0)
    c: Equal(g1,g2)
    c: DistanceY(g1,g1) = 40
FEATURE [PartDesign::Pad] Pad023  label="Decoration, Left, Cut, Bottom002"
  Direction = (0,-1,2e-16)
  Length = 40
  Length2 = 10
  Placement = pos=(0,0,0) rot=(1,0,0;1.5708rad)
  Profile = -> Sketch023
  ReferenceAxis = -> Sketch023 [N_Axis]
  SideType = 0
  Suppressed = false
  Type = 0
  Type2 = 0
FEATURE [PartDesign::Body] Body023  label="Body, Decoration, Left, Cut, Bottom002"
  AllowCompound = true
  Group = -> [Sketch023,Pad023]
  Origin = -> Origin032
  Tip = -> Pad023
FEATURE [Sketcher::SketchObject] Sketch024  label="Pattern, Decoration, Left, Cut, Top002"
  ArcFitTolerance = 0
  AttachmentOffset = pos=(60,690,0) rot=(0,0,1;0rad)
  AttachmentSupport = -> [XZ_Plane032]
  ExternalTypes = [0]
  FullyConstrained = true
  MakeInternals = false
  MapMode = 5
  Placement = pos=(60,1.532e-13,690) rot=(1,0,0;1.5708rad)
  _ExternalGeoVersion = 0
  expr: .AttachmentOffset.Base.x = Spreadsheet002.fldoffset
  expr: .AttachmentOffset.Base.y = Spreadsheet002.flfheight - Spreadsheet002.fldoffset
  sketch-geometry (3):
    g0: LineSegment StartX=0 StartY=0 StartZ=0 EndX=40 EndY=-40 EndZ=0
    g1: LineSegment StartX=40 StartY=-40 StartZ=0 EndX=40 EndY=0 EndZ=0
    g2: LineSegment StartX=40 StartY=0 StartZ=0 EndX=0 EndY=0 EndZ=0
  constraints (8):
    c: Coincident(g-1,g0)
    c: Coincident(g0,g1)
    c: PointOnObject(g1,g-1)
    c: Vertical(g1)
    c: Coincident(g1,g2)
    c: Coincident(g2,g0)
    c: Equal(g1,g2)
    c: DistanceY(g1,g1) = 40
FEATURE [PartDesign::Pad] Pad024  label="Decoration, Left, Cut, Top002"
  Direction = (0,-1,2e-16)
  Length = 40
  Length2 = 10
  Placement = pos=(0,0,0) rot=(1,0,0;1.5708rad)
  Profile = -> Sketch024
  ReferenceAxis = -> Sketch024 [N_Axis]
  SideType = 0
  Suppressed = false
  Type = 0
  Type2 = 0
FEATURE [PartDesign::Body] Body024  label="Body, Decoration, Left, Cut, Top002"
  AllowCompound = true
  Group = -> [Sketch024,Pad024]
  Origin = -> Origin033
  Tip = -> Pad024
COMPONENT P17 — recipe-attached ("Part, Handle002", modeled in this document).
Construction recipe (the document's own serialized feature program — sketch geometry with constraints, then the solid features built on it; lengths are millimeters unless a unit is written):

FEATURE [Sketcher::SketchObject] Sketch025
  ArcFitTolerance = 0
  AttachmentOffset = pos=(30,375,8) rot=(0,0,1;0rad)
  AttachmentSupport = -> [XZ_Plane034]
  ExternalTypes = [0]
  FullyConstrained = true
  MakeInternals = false
  MapMode = 5
  Placement = pos=(30,-8,375) rot=(1,0,0;1.5708rad)
  _ExternalGeoVersion = 0
  expr: .AttachmentOffset.Base.x = Spreadsheet002.fldoffset / 2
  expr: .AttachmentOffset.Base.y = Spreadsheet002.flfheight / 2
  sketch-geometry (13):
    g0: LineSegment StartX=-2.89 StartY=0 StartZ=0 EndX=-2.89 EndY=-20 EndZ=0
    g1: LineSegment StartX=2.89 StartY=0 StartZ=0 EndX=2.89 EndY=-20 EndZ=0
    g2: LineSegment StartX=-2.89 StartY=0 StartZ=0 EndX=2.89 EndY=0 EndZ=0
    g3: LineSegment StartX=-2.89 StartY=-20 StartZ=0 EndX=-20.5255 EndY=-49.48 EndZ=0
    g4: LineSegment StartX=2.89 StartY=-20 StartZ=0 EndX=20.5255 EndY=-49.48 EndZ=0
    g5: LineSegment StartX=-13.7655 StartY=-48.2802 StartZ=0 EndX=0 EndY=-23.6879 EndZ=0
    g6: LineSegment StartX=0 StartY=-23.6879 StartZ=0 EndX=13.7655 EndY=-48.2802 EndZ=0
    g7: ArcOfCircle CenterX=-7.79 CenterY=-51.47 CenterZ=0 NormalX=0 NormalY=0 NormalZ=1 AngleXU=0 Radius=12.89 StartAngle=2.98659 EndAngle=4.71316
    g8: ArcOfCircle CenterX=-7.79 CenterY=-51.47 CenterZ=0 NormalX=0 NormalY=0 NormalZ=1 AngleXU=0 Radius=6.77356 StartAngle=2.65126 EndAngle=4.1959
    g9: ArcOfCircle CenterX=0 CenterY=-62.5379 CenterZ=0 NormalX=0 NormalY=0 NormalZ=1 AngleXU=0 Radius=12.28 StartAngle=0.435264 EndAngle=2.70633
    g10: ArcOfCircle CenterX=7.79 CenterY=-51.47 CenterZ=0 NormalX=0 NormalY=0 NormalZ=1 AngleXU=0 Radius=6.77356 StartAngle=5.22888 EndAngle=6.77352
    g11: ArcOfCircle CenterX=7.79 CenterY=-51.47 CenterZ=0 NormalX=0 NormalY=0 NormalZ=1 AngleXU=0 Radius=12.89 StartAngle=4.71316 EndAngle=6.43819
    g12: LineSegment StartX=-7.78 StartY=-64.36 StartZ=0 EndX=7.8 EndY=-64.36 EndZ=0
  constraints (42):
    c: PointOnObject(g0,g-1)
    c: Vertical(g0)
    c: PointOnObject(g1,g-1)
    c: Vertical(g1)
    c: Coincident(g2,g0)
    c: Coincident(g2,g1)
    c: Coincident(g3,g0)
    c: Coincident(g4,g1)
    c: PointOnObject(g5,g-2)
    c: Coincident(g6,g5)
    c: Coincident(g7,g3)
    c: Coincident(g8,g5)
    c: Coincident(g9,g8)
    c: Coincident(g10,g9)
    c: Coincident(g10,g6)
    c: Coincident(g11,g4)
    c: Coincident(g12,g7)
    c: Coincident(g12,g11)
    c: Horizontal(g12)
    c: DistanceY(g1,g1) = 20
    c: Equal(g0,g1)
    c: Equal(g3,g4)
    c: Equal(g5,g6)
    c: Equal(g8,g10)
    c: Equal(g7,g11)
    c: PointOnObject(g9,g-2)
    c: Horizontal(g9,g8)
    c: Horizontal(g3,g4)
    c: Horizontal(g5,g6)
    c: Coincident(g7,g8)
    c: Coincident(g10,g11)
    c: DistanceX(g0,g-1) = 2.89
    c: DistanceX(g3,g5) = 6.76
    c: DistanceY(g9,g5) = 38.85
    c: DistanceY(g7,g-1) = 64.36
    c: DistanceY(g7,g-1) = 51.47
    c: DistanceX(g8,g9) = 22.27
    c: DistanceX(g9,g10) = 7.79
    c: DistanceY(g9,g-1) = 57.36
    c: DistanceY(g4,g-1) = 49.48
    c: DistanceX(g9,g11) = 7.8
    c: Radius(g9) = 12.28
FEATURE [PartDesign::Pad] Pad025  label="Handle002"
  Direction = (0,-1,2e-16)
  Length = 5
  Length2 = 10
  Placement = pos=(0,0,0) rot=(1,0,0;1.5708rad)
  Profile = -> Sketch025
  ReferenceAxis = -> Sketch025 [N_Axis]
  SideType = 0
  Suppressed = false
  Type = 0
  Type2 = 0
FEATURE [PartDesign::Body] Body025  label="Body, Handle002"
  AllowCompound = true
  Group = -> [Sketch025,Pad025]
  Origin = -> Origin035
  Tip = -> Pad025
PROVENANCE & LICENSES
A FreeCAD (.FCStd) document from a public repository crawl; recipes are the document's own serialized feature recipes (and, for linked parts, companion documents' recipes).
License: mit.
